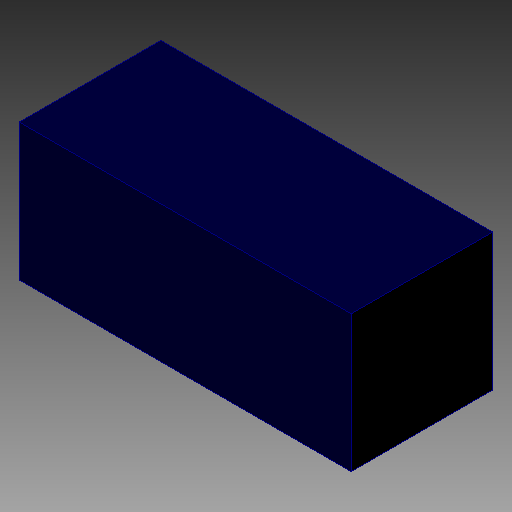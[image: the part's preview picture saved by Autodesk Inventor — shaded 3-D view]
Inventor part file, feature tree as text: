
AUTODESK INVENTOR PART (.ipt)
format: ipt  version: 2018 (Build 220112000, 112)  size: 80,384 bytes
history: native  units: in
note: dims shown in document units (in); Inventor stores cm internally (conversion verified against a paired STEP export)
features: extrude x1
ambient origin geometry x8: Origin, YZ Plane, XZ Plane, XY Plane, X Axis, Y Axis, Z Axis, Center Point
bodies: Solid1 (feature_tree)
feature tree (1):
  extrude  "Extrusion1"  Depth=0.0394in TaperAngle=0.0deg
